# Revit family: Pro_Filtration_Bottle_Filling _Station_Single_ADA-Elkay-LZS8WSBPRO_FLP4_FSR5_UV
name_source: partatom
category: Plumbing Fixtures
units: mm (PartAtom-declared; Revit-internal decimal feet)

## family parameters
Always vertical = Yes
Cut with Voids When Loaded = No
Maintain Annotation Orientation = No
OmniClass Number = 23.65.70.14.11
OmniClass Title = Drinking Fountains/Coolers
Part Type = Normal
Room Calculation Point = No
Round Connector Dimension = Use Diameter
Shared = No
Work Plane-Based = No

## types (4) — shared parameters
Activation Method = Electronic Bottle Filler Sensor with Electronic Front and Side Bubbler Pushbar
Approx. Shipping Weight (lbs) = 79
Assembly Code = D2010810
Chilling Capacity (GPH) = 8
Connector Outlet B = 1.25 "
Connector Supply A = 0.375 "
Current = 0 A
Inlet Connection Size (inch) = 0.375 "
Main Material = Finish-Elkay-Steel
Manufacturer = Elkay Manufacturer Company
Manufacturer Brand = Elkay (by Zurn Elkay Water Solutions)
Masking Arc Radius = 21 "
Material_Basin = Finish-Elkay-Steel
Material_Bottle Filler = Finish-Elkay-Midnight Black
Material_Bubbler = Finish-Elkay-Midnight Black
Material_Display = Finish-Elkay-Gray
Material_Shroud = Finish-Elkay-Midnight Black
Material_Wrapper = Finish-Elkay-Midnight Black
Number of Poles = 1
Outlet Connection Size (inch) = 1.25 "
Power Factor = 1
Product Documentation Link = https://www.elkayfiles.com
Product Installation Sheet URL = https://www.elkayfiles.com
Product Page URL = https://www.elkay.com
Product Weight (lbs) = 74
Product data URL = https://www.bimobject.com
Repair Parts URL = https://www.elkayfiles.com
URL = https://www.elkay.com
Voltage = 115 V
zero-valued in all types: CWFU, Default Elevation, HWFU, WFU

## per-type parameters (varying)
| type | Description | Model |
| LZS8WSBPRO (Bottle Filling Station & Single ADA Cooler Refrigerated ) | Elkay Pro Filtration Bottle Filling Station & Single ADA Cooler Refrigerated Ultra Capacity Lead Reduction | LZS8WSBPRO |
| LZS8WSBPRO-FSR5  (Bottle Filling Station & Single ADA Cooler Refrigerated  ) | Elkay Pro Filtration® Bottle Filling Station & Single ADA Cooler Refrigerated Ultra-Capacity Lead + Sediment Prefilter | LZS8WSBPRO-FSR5 |
| LZS8WSBPRO-FLP4  (Bottle Filling Station & Single ADA Cooler Refrigerated  ) | Elkay Pro Filtration® Bottle Filling Station & Single ADA Cooler Refrigerated Total PFAS* + Lead Reduction | LZS8WSBPRO-FLP4 |
| LZS8WSBPRO-UV  (Bottle Filling Station & Single ADA Cooler Refrigerated  ) | Elkay Pro Filtration® Bottle Filling Station & Single ADA Cooler Refrigerated Ultra-Capacity Lead + UV Protection | LZS8WSBPRO-UV |

## geometry (parser evidence)
native form markers: Sweep x9
no freeform markers — native parametric forms only
